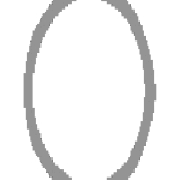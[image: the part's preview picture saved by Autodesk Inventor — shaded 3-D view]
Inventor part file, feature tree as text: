
AUTODESK INVENTOR PART (.ipt)
format: ipt  version: 2021 (Build 250183000, 183)  size: 111,616 bytes
history: native  units: in
note: dims shown in document units (in); Inventor stores cm internally (conversion verified against a paired STEP export)
features: other x4, sketch x3, plane x1
ambient origin geometry x8: Origin, YZ Plane, XZ Plane, XY Plane, X Axis, Y Axis, Z Axis, Center Point
bodies: Solid1 (feature_tree), Body (feature_tree)
feature tree (8):
  other  "Driven Length"
  other  "Frame Generator"
  other  "Start Plane"
  other  "End Plane"
  sketch  "Sketch"  dims[d2=40.658in d4=-0.0in d5=40.658in d6=0.12in d7=0.0in d8=90.0deg d9=40.658in]
  sketch  "Sketch2"  dims[d0=1.0in]
  plane  "Work Plane3"
  sketch  "Sketch3"  dims[d1=0.065in]
